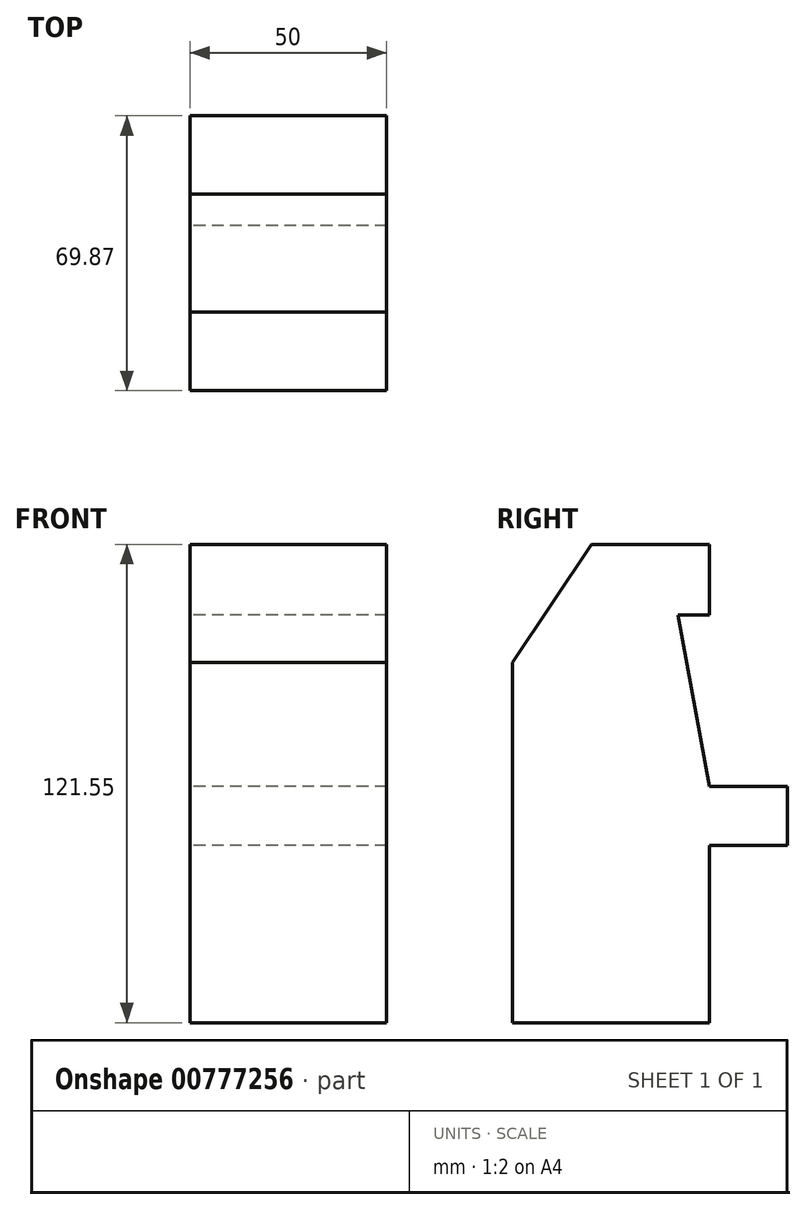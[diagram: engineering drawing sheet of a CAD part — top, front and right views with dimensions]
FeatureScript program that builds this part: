
annotation { "Feature Type Name" : "Feature", "Feature Type Description" : "" }
export const myFeature = defineFeature(function(context is Context, id is Id, definition is map)
    precondition{}
    {
        {
            var Q0;
            Q0=qCreatedBy(makeId("Right.planeOp"),FACE);
            var sketch = newSketch(context, id + "F0", { "sketchPlane" : qUnion([Q0])});
            skLineSegment(sketch, "E0.bottom", {"start": v(25, 0) * mm, "end": v(-25, 0) * mm});
            skLineSegment(sketch, "E0.top", {"start": v(25, 121.55) * mm, "end": v(-5, 121.55) * mm});
            skLineSegment(sketch, "E0.left", {"start": v(25, 0) * mm, "end": v(25, 45) * mm});
            skLineSegment(sketch, "E0.right", {"start": v(-25, 0) * mm, "end": v(-25, 91.55) * mm});
            skPoint(sketch, "E0.middle", {"position": v(0, 60.77) * mm});
            skLineSegment(sketch, "E1.bottom", {"start": v(25, 45) * mm, "end": v(44.87, 45) * mm});
            skLineSegment(sketch, "E1.top", {"start": v(25, 60) * mm, "end": v(44.87, 60) * mm});
            skLineSegment(sketch, "E1.right", {"start": v(44.87, 45) * mm, "end": v(44.87, 60) * mm});
            skLineSegment(sketch, "E2", {"start": v(-5, 121.55) * mm, "end": v(-25, 91.55) * mm});
            skLineSegment(sketch, "E3", {"start": v(25, 103.55) * mm, "end": v(17, 103.55) * mm});
            skLineSegment(sketch, "E4", {"start": v(17, 103.55) * mm, "end": v(25, 60) * mm});
            skPoint(sketch, "E5.orphan", {"position": v(-25, 121.55) * mm});
            skLineSegment(sketch, "E6.trimOffspring", {"start": v(25, 103.55) * mm, "end": v(25, 121.55) * mm});
            skSolve(sketch);
        }
        {
            var Q0;
            Q0=makeQuery(id+"F0.imprint","IMPRINT",FACE,{"disambiguationData":[TD([[makeQuery(id+"F0.imprint","IMPRINT",EDGE,{"derivedFrom":sQuery(id+"F0.wireOp",EDGE,"E0.bottom")}),-1.0]])]});
            extrude(context, id + "F1", {"entities" : qUnion([Q0]), "endBound" : BoundingType.SYMMETRIC, "depth" : 50 * mm, "offsetDistance" : 25 * mm});
        }
    });
